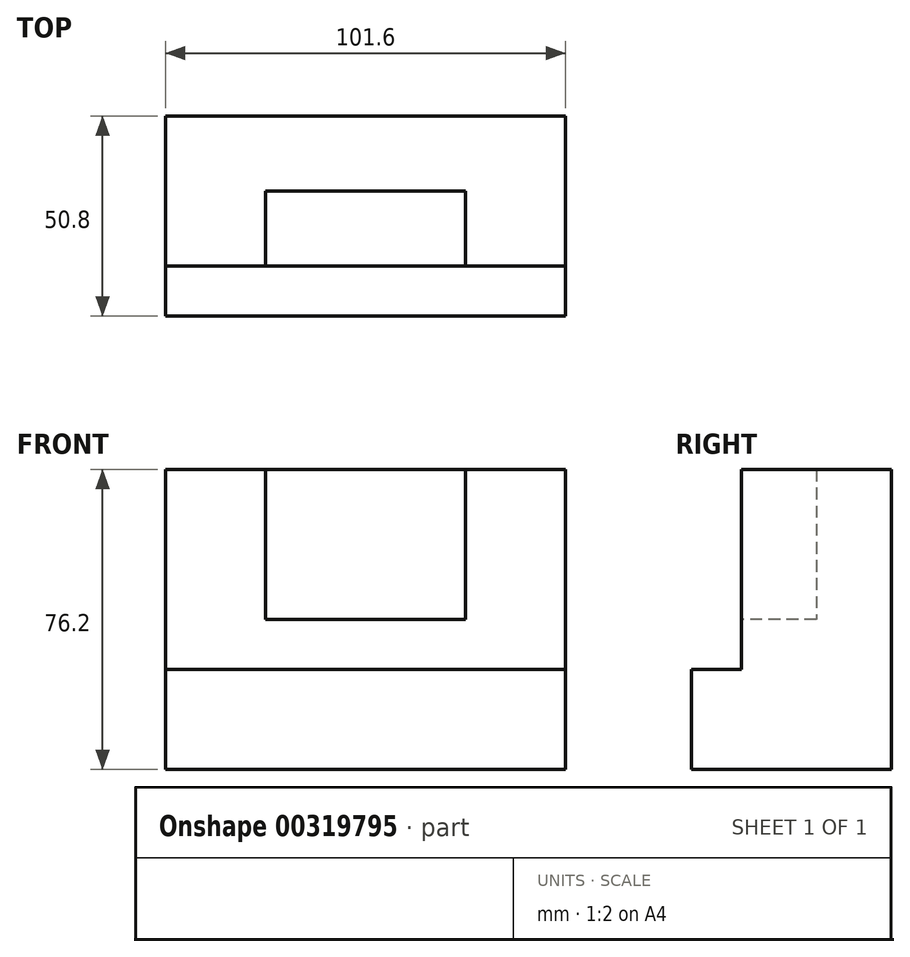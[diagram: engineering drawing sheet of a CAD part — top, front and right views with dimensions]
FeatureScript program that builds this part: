
annotation { "Feature Type Name" : "Feature", "Feature Type Description" : "" }
export const myFeature = defineFeature(function(context is Context, id is Id, definition is map)
    precondition{}
    {
        {
            var Q0;
            Q0=qCreatedBy(makeId("Top.planeOp"),FACE);
            var sketch = newSketch(context, id + "F0", { "sketchPlane" : qUnion([Q0])});
            skLineSegment(sketch, "E0", {"start": v(-25.53, -13.26) * mm, "end": v(76.07, -13.26) * mm});
            skLineSegment(sketch, "E1", {"start": v(76.07, -13.26) * mm, "end": v(76.07, 37.54) * mm});
            skLineSegment(sketch, "E2", {"start": v(76.07, 37.54) * mm, "end": v(-25.53, 37.54) * mm});
            skLineSegment(sketch, "E3", {"start": v(-25.53, 37.54) * mm, "end": v(-25.53, -13.26) * mm});
            skSolve(sketch);
        }
        {
            var Q0;
            Q0=makeQuery(id+"F0.imprint","IMPRINT",FACE,{"disambiguationData":[TD([[makeQuery(id+"F0.imprint","IMPRINT",EDGE,{"derivedFrom":sQuery(id+"F0.wireOp",EDGE,"E0")}),1.0]])]});
            extrude(context, id + "F1", {"entities" : qUnion([Q0]), "depth" : 25.4 * mm});
        }
        {
            var Q0;
            Q0=makeQuery(id+"F1.opExtrude","CAP_FACE",FACE,{"disambiguationData":[OSD([sQuery(id+"F0.wireOp",EDGE,"E0"),sQuery(id+"F0.wireOp",EDGE,"E1"),sQuery(id+"F0.wireOp",EDGE,"E2"),sQuery(id+"F0.wireOp",EDGE,"E3")])],"isStart":false});
            var sketch = newSketch(context, id + "F2", { "sketchPlane" : qUnion([Q0])});
            skLineSegment(sketch, "E4", {"start": v(-25.53, 37.54) * mm, "end": v(-25.53, -0.56) * mm});
            skLineSegment(sketch, "E5", {"start": v(-25.53, -0.56) * mm, "end": v(76.07, -0.56) * mm});
            skLineSegment(sketch, "E6", {"start": v(76.07, -0.56) * mm, "end": v(76.07, 37.54) * mm});
            skLineSegment(sketch, "E7", {"start": v(76.07, 37.54) * mm, "end": v(-25.53, 37.54) * mm});
            skSolve(sketch);
        }
        {
            var Q0;
            Q0=makeQuery(id+"F2.imprint","IMPRINT",FACE,{"disambiguationData":[TD([[makeQuery(id+"F2.imprint","IMPRINT",EDGE,{"derivedFrom":sQuery(id+"F2.wireOp",EDGE,"E4")}),1.0]])]});
            extrude(context, id + "F3", {"entities" : qUnion([Q0]), "operationType" : NewBodyOperationType.ADD, "depth" : 50.8 * mm});
        }
        {
            var Q0;
            Q0=makeQuery(id+"F3.opExtrude","SWEPT_FACE",FACE,{"disambiguationData":[OSD([sQuery(id+"F2.wireOp",EDGE,"E5")])]});
            var sketch = newSketch(context, id + "F4", { "sketchPlane" : qUnion([Q0])});
            skLineSegment(sketch, "E8.bottom", {"start": v(-0.13, 76.2) * mm, "end": v(50.67, 76.2) * mm});
            skLineSegment(sketch, "E8.top", {"start": v(-0.13, 38.1) * mm, "end": v(50.67, 38.1) * mm});
            skLineSegment(sketch, "E8.left", {"start": v(-0.13, 76.2) * mm, "end": v(-0.13, 38.1) * mm});
            skLineSegment(sketch, "E8.right", {"start": v(50.67, 76.2) * mm, "end": v(50.67, 38.1) * mm});
            skSolve(sketch);
        }
        {
            var Q0;
            Q0=makeQuery(id+"F4.imprint","IMPRINT",FACE,{"disambiguationData":[TD([[makeQuery(id+"F4.imprint","IMPRINT",EDGE,{"derivedFrom":sQuery(id+"F4.wireOp",EDGE,"E8.bottom")}),-1.0]])]});
            extrude(context, id + "F5", {"entities" : qUnion([Q0]), "operationType" : NewBodyOperationType.REMOVE, "oppositeDirection" : true, "depth" : 19.05 * mm});
        }
    });
